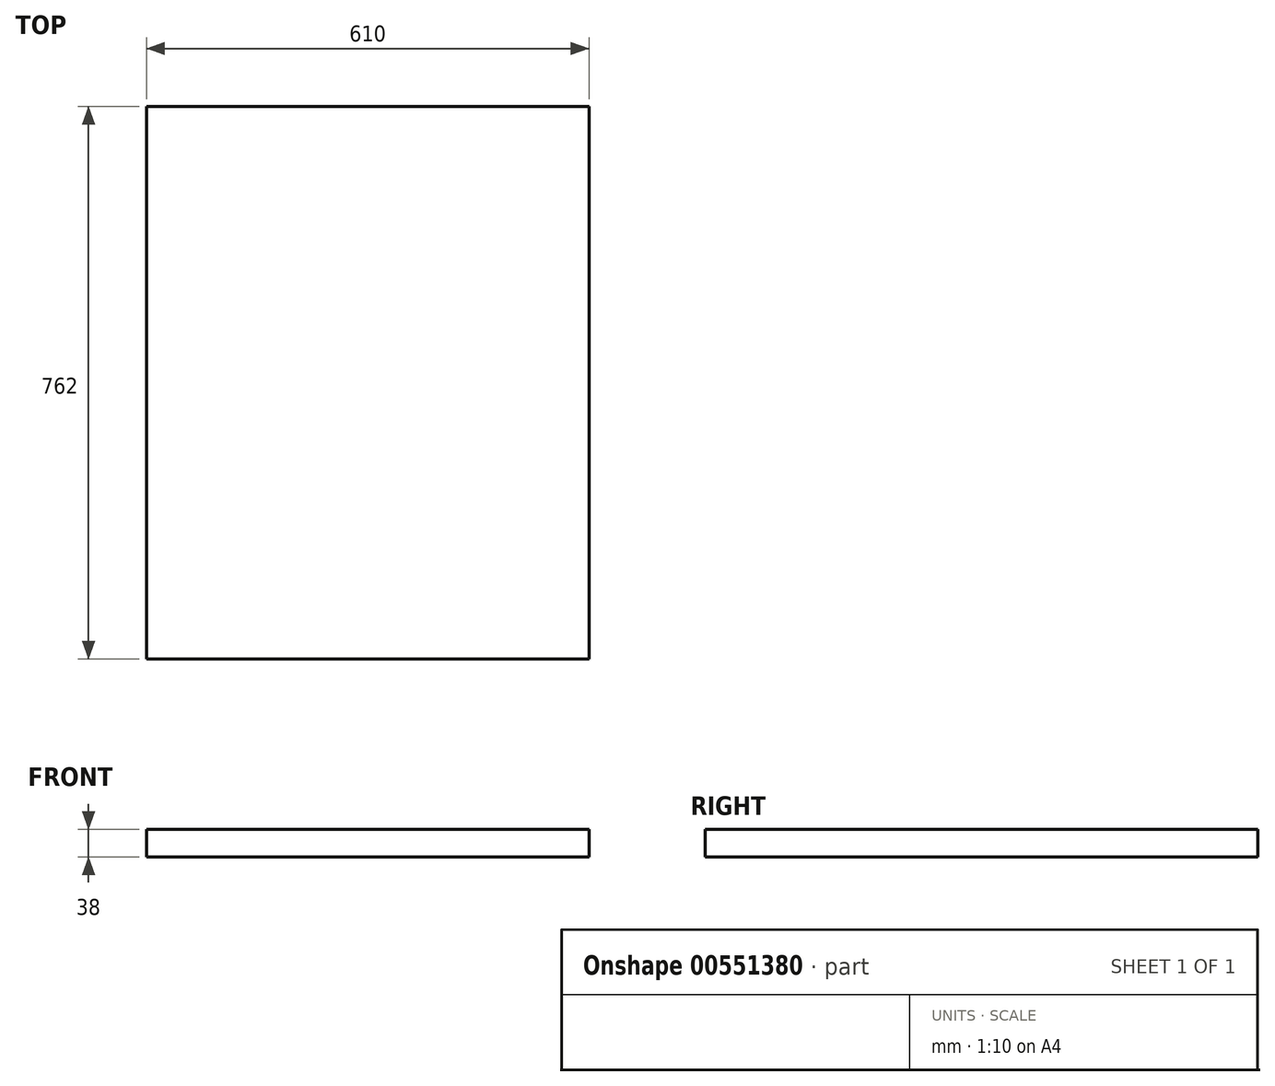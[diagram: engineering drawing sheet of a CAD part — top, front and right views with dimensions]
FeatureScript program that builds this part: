
annotation { "Feature Type Name" : "Feature", "Feature Type Description" : "" }
export const myFeature = defineFeature(function(context is Context, id is Id, definition is map)
    precondition{}
    {
        {
            var Q0;
            Q0=qCreatedBy(makeId("Top.planeOp"),FACE);
            var sketch = newSketch(context, id + "F0", { "sketchPlane" : qUnion([Q0])});
            skLineSegment(sketch, "E0.bottom", {"start": v(305, -381) * mm, "end": v(-305, -381) * mm});
            skLineSegment(sketch, "E0.top", {"start": v(305, 381) * mm, "end": v(-305, 381) * mm});
            skLineSegment(sketch, "E0.left", {"start": v(305, -381) * mm, "end": v(305, 381) * mm});
            skLineSegment(sketch, "E0.right", {"start": v(-305, -381) * mm, "end": v(-305, 381) * mm});
            skPoint(sketch, "E0.middle", {"position": v(0, 0) * mm});
            skSolve(sketch);
        }
        {
            var Q0;
            Q0=makeQuery(id+"F0.imprint","IMPRINT",FACE,{"disambiguationData":[TD([[makeQuery(id+"F0.imprint","IMPRINT",EDGE,{"derivedFrom":sQuery(id+"F0.wireOp",EDGE,"E0.bottom")}),-1.0]])]});
            extrude(context, id + "F1", {"entities" : qUnion([Q0]), "depth" : 38 * mm, "offsetDistance" : 25 * mm});
        }
    });
